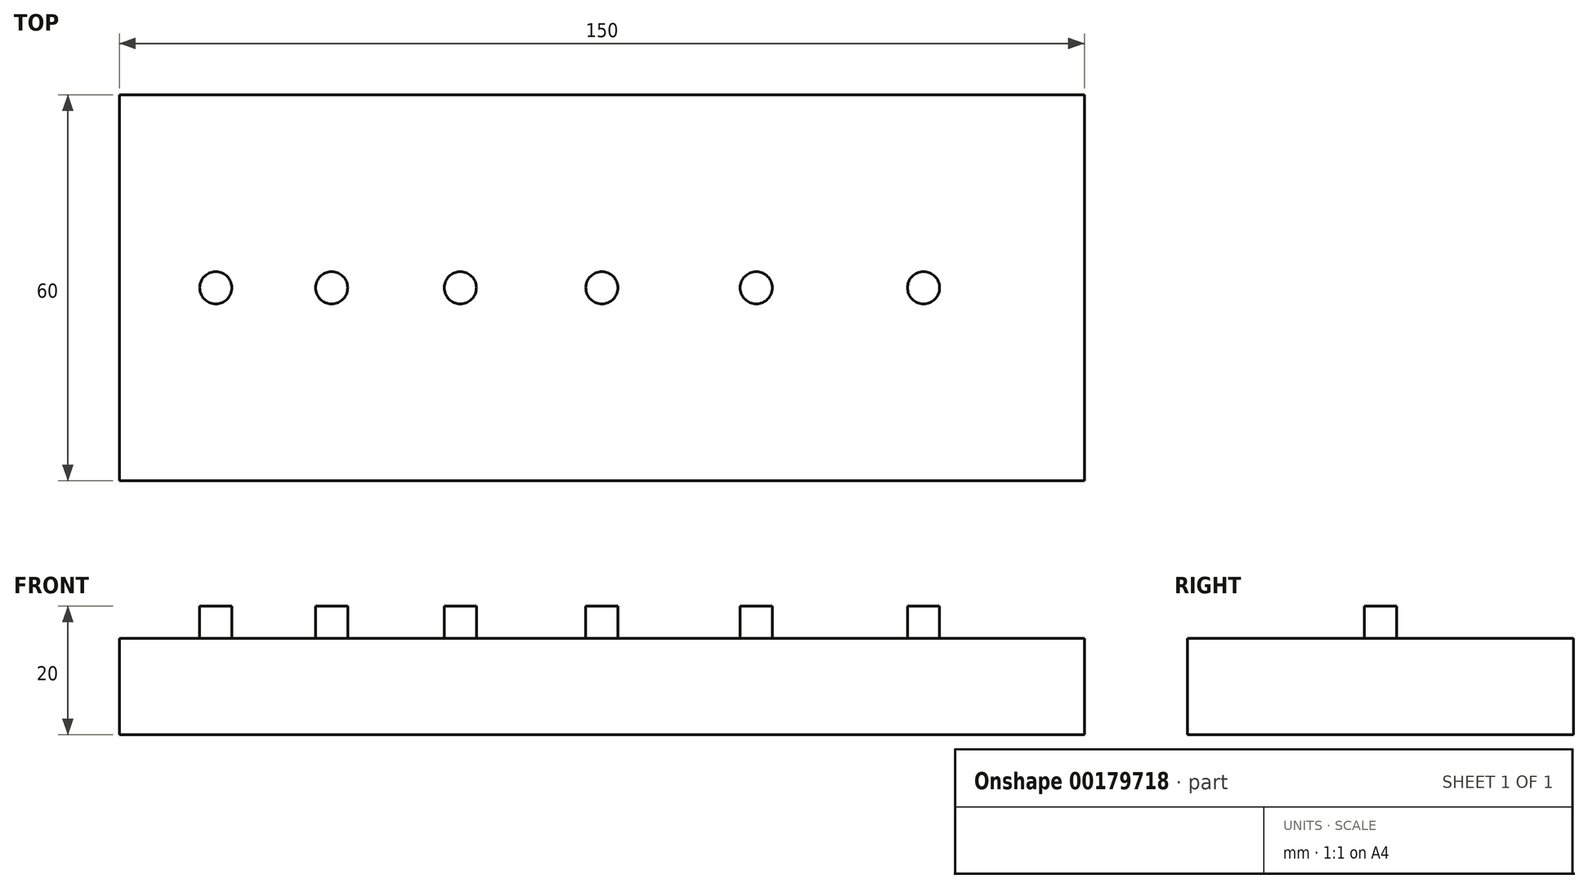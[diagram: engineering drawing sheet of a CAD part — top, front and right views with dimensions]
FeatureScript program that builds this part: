
annotation { "Feature Type Name" : "Feature", "Feature Type Description" : "" }
export const myFeature = defineFeature(function(context is Context, id is Id, definition is map)
    precondition{}
    {
        {
            var Q0;
            Q0=qCreatedBy(makeId("Top.planeOp"),FACE);
            var sketch = newSketch(context, id + "F0", { "sketchPlane" : qUnion([Q0])});
            skLineSegment(sketch, "E0.bottom", {"start": v(-58.81, 27.85) * mm, "end": v(91.19, 27.85) * mm});
            skLineSegment(sketch, "E0.top", {"start": v(-58.81, -32.15) * mm, "end": v(91.19, -32.15) * mm});
            skLineSegment(sketch, "E0.left", {"start": v(-58.81, 27.85) * mm, "end": v(-58.81, -32.15) * mm});
            skLineSegment(sketch, "E0.right", {"start": v(91.19, 27.85) * mm, "end": v(91.19, -32.15) * mm});
            skSolve(sketch);
        }
        {
            var Q0;
            Q0 = qSketchRegion(id + "F0", true);
            extrude(context, id + "F1", {"entities" : qUnion([Q0]), "depth" : 15 * mm});
        }
        {
            var Q0;
            Q0=makeQuery(id+"F1.opExtrude","CAP_FACE",FACE,{"disambiguationData":[OSD([sQuery(id+"F0.wireOp",EDGE,"E0.bottom"),sQuery(id+"F0.wireOp",EDGE,"E0.top"),sQuery(id+"F0.wireOp",EDGE,"E0.left"),sQuery(id+"F0.wireOp",EDGE,"E0.right")])],"isStart":false});
            var sketch = newSketch(context, id + "F2", { "sketchPlane" : qUnion([Q0])});
            skCircle(sketch, "E1", {"center": v(-43.81, -2.15) * mm, "radius": 2.5 * mm});
            skCircle(sketch, "E2", {"center": v(-25.81, -2.15) * mm, "radius": 2.5 * mm});
            skCircle(sketch, "E3", {"center": v(-5.81, -2.15) * mm, "radius": 2.5 * mm});
            skCircle(sketch, "E4", {"center": v(16.19, -2.15) * mm, "radius": 2.5 * mm});
            skCircle(sketch, "E5", {"center": v(40.19, -2.15) * mm, "radius": 2.5 * mm});
            skCircle(sketch, "E6", {"center": v(66.19, -2.15) * mm, "radius": 2.5 * mm});
            skSolve(sketch);
        }
        {
            var Q0;
            Q0 = qSketchRegion(id + "F2", true);
            extrude(context, id + "F3", {"entities" : qUnion([Q0]), "operationType" : NewBodyOperationType.ADD, "depth" : 5 * mm});
        }
    });
